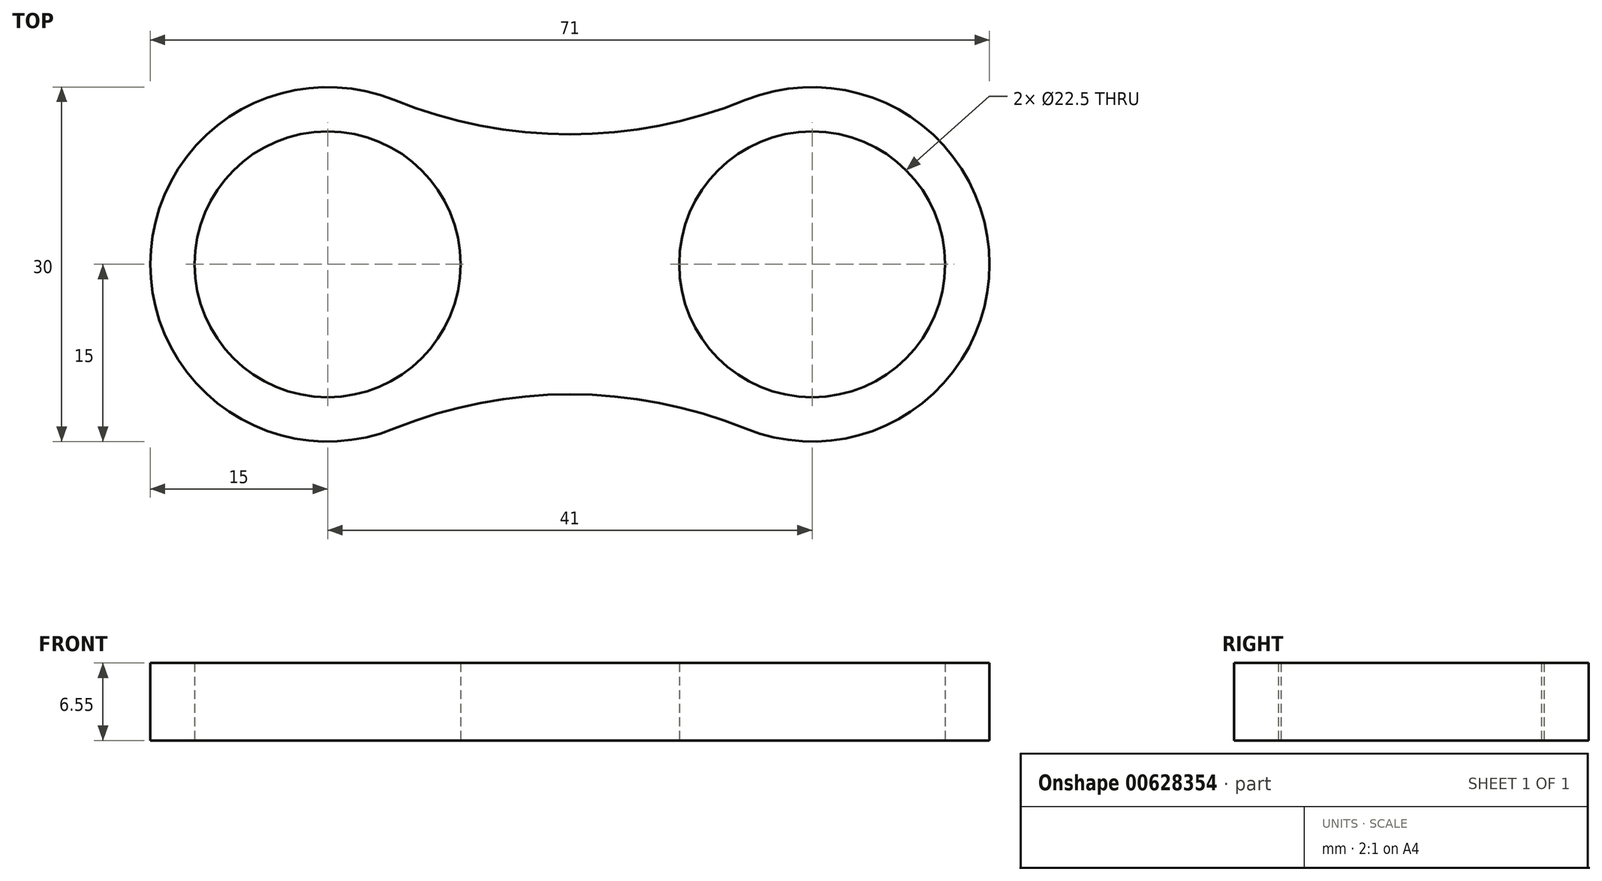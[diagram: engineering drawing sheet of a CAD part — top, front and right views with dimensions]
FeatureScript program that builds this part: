
annotation { "Feature Type Name" : "Feature", "Feature Type Description" : "" }
export const myFeature = defineFeature(function(context is Context, id is Id, definition is map)
    precondition{}
    {
        {
            var Q0;
            Q0=qCreatedBy(makeId("Top.planeOp"),FACE);
            var sketch = newSketch(context, id + "F0", { "sketchPlane" : qUnion([Q0])});
            skCircle(sketch, "E0", {"center": v(0, 0) * mm, "radius": 11.25 * mm});
            skArc(sketch, "E1", {"start": v(-5.63, -13.9) * mm, "mid": v(15, 0) * mm, "end": v(-5.63, 13.9) * mm});
            skCircle(sketch, "E2", {"center": v(-41, 0) * mm, "radius": 11.25 * mm});
            skArc(sketch, "E3", {"start": v(-35.37, 13.9) * mm, "mid": v(-56, 0) * mm, "end": v(-35.37, -13.9) * mm});
            skArc(sketch, "E4", {"start": v(-35.37, 13.9) * mm, "mid": v(-20.5, 11) * mm, "end": v(-5.63, 13.9) * mm});
            skArc(sketch, "E5.MirrorCS", {"start": v(-35.37, -13.9) * mm, "mid": v(-20.5, -11) * mm, "end": v(-5.63, -13.9) * mm});
            skSolve(sketch);
        }
        {
            var Q0;
            Q0 = qSketchRegion(id + "F0", true);
            extrude(context, id + "F1", {"entities" : qUnion([Q0]), "depth" : 6.55 * mm, "offsetDistance" : 25 * mm});
        }
    });
